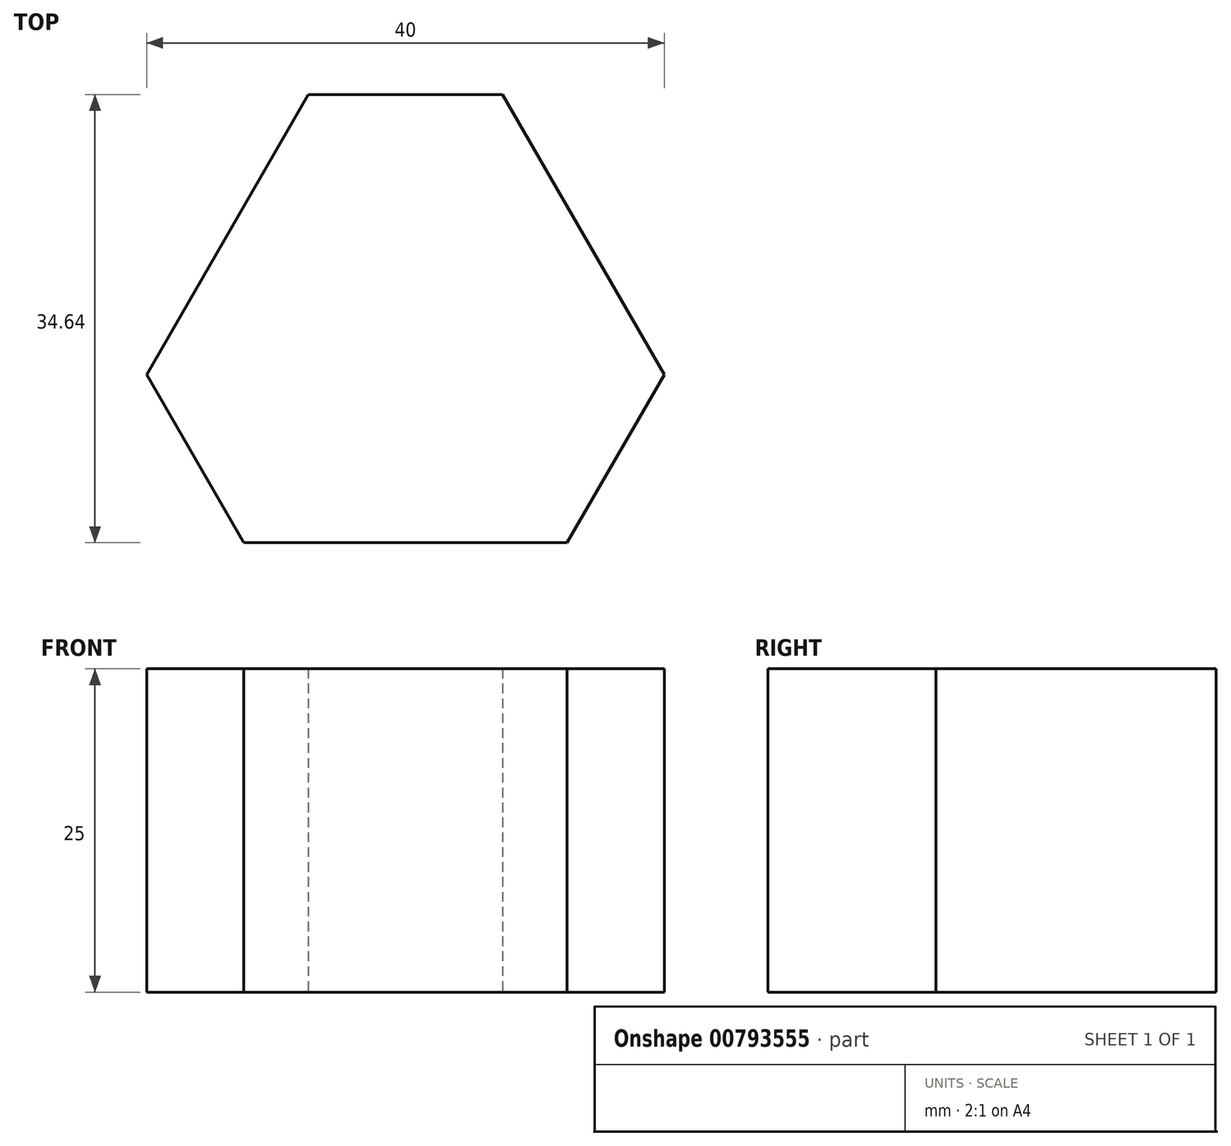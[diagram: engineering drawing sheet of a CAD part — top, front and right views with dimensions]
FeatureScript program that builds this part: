
annotation { "Feature Type Name" : "Feature", "Feature Type Description" : "" }
export const myFeature = defineFeature(function(context is Context, id is Id, definition is map)
    precondition{}
    {
        {
            var Q0;
            Q0=qCreatedBy(makeId("Top.planeOp"),FACE);
            var sketch = newSketch(context, id + "F0", { "sketchPlane" : qUnion([Q0])});
            skLineSegment(sketch, "E0", {"start": v(-40.73, -5.2) * mm, "end": v(-45.46, -13.4) * mm});
            skLineSegment(sketch, "E1", {"start": v(17.6, -5.2) * mm, "end": v(20.25, -9.8) * mm});
            skLineSegment(sketch, "E2", {"start": v(-55.68, -5.2) * mm, "end": v(-40.73, -5.2) * mm});
            skLineSegment(sketch, "E3.trimOffspring", {"start": v(-10.92, 45.32) * mm, "end": v(-8.84, 48.92) * mm});
            skLineSegment(sketch, "E4.trimOffspring", {"start": v(-40.73, -5.2) * mm, "end": v(-55.68, -5.2) * mm});
            skLineSegment(sketch, "E5.trimOffspring", {"start": v(17.6, -5.2) * mm, "end": v(38.1, -5.2) * mm});
            skLineSegment(sketch, "E6.trimOffspring", {"start": v(-10.92, 45.32) * mm, "end": v(-10.92, 48.65) * mm, "construction": true});
            skLineSegment(sketch, "E7", {"start": v(51.64, 47.6) * mm, "end": v(36.64, 47.6) * mm});
            skLineSegment(sketch, "E8", {"start": v(36.64, 47.6) * mm, "end": v(24.14, 25.95) * mm});
            skLineSegment(sketch, "E9", {"start": v(24.14, 25.95) * mm, "end": v(31.64, 12.96) * mm});
            skLineSegment(sketch, "E10", {"start": v(31.64, 12.96) * mm, "end": v(56.64, 12.96) * mm});
            skLineSegment(sketch, "E11", {"start": v(56.64, 12.96) * mm, "end": v(64.14, 25.95) * mm});
            skLineSegment(sketch, "E12", {"start": v(64.14, 25.95) * mm, "end": v(51.64, 47.6) * mm});
            skSolve(sketch);
        }
        {
            var Q0;
            Q0 = qSketchRegion(id + "F0", true);
            extrude(context, id + "F1", {"entities" : qUnion([Q0]), "depth" : 25 * mm, "offsetDistance" : 25 * mm});
        }
    });
